# Revit family: Doors_Sliding-Doors_Krownlab_Loki_Single-Sliding-Doors1
name_source: partatom
category: Doors
revit_build: Autodesk Revit 2017 (Build: 20190508_0315(x64)
units: mm (PartAtom-declared; Revit-internal decimal feet)

## family parameters
Always vertical = Yes
Cut with Voids When Loaded = No
Host = Wall
OmniClass Number = 23.30.10.00
OmniClass Title = Doors
Room Calculation Point = No
Shared = No

## types (1)
- Refer to Type Catalog
    Analytic Construction = <None>
    Assembly Code = C1020
    Clnc = 1 1/8"
    Custom Overlap Left = 2"
    Custom Overlap Right = 2"
    Custom Overlap Top = 1 1/4"
    Default Door Thickness = Default Thickness is 1 3/4 inches
    Description = A completely customizable sliding door hardware system with out-of-level and out-of-plum adjustment at every attachment point.
    Door Thickness Restrictions = Top Mount door panel thickness range is: 1-3/8” – 3”. Face Mount door panel thickness range is: 3/4” – 2-1/2”. Glass Mount door panel thickness range is: 3/8” – ½”.
    Edition number = 2
    Face Mount = Default Thickness is 1 3/4 inches
    Function = Interior
    Glass Mount = Default Thickness is 1/2 inch
    Glass Weight Calculation = 0.00 lb
    Height = 90 11/16"
    Lft_Sd_Ctrl = 2"
    Manufacturer = Krownlab
    Model = Loki Single Door
    Mounting Point Spacing = 24"
    Operation = Sliding
    Panel Area = 21.22 ft²
    Panel Height = 84 7/8"
    Panel Material = Wood - Krownlab - Showcase Wood
    Panel Size Availability = Available
    Panel Size Restrictions = Minimum Panel Height is 20”, Minimum Panel Width is 24”.
    Panel Width = 36"
    Product Guid = 76f97f46-7ea8-410c-a3bf-36cbabb0e76b
    Product data url = https://bimobject.com
    Rough Height = 84"
    Rough Width = 32"
    Rt_Sd_Ctrl = 2"
    Standard Glass Weights = 3/8” glass weighs ~5lb/sf. ½” glass weighs ~6.5lb/sf
    Standoff 1 = Krownlab Track Standoff : Solid Wall - 1/4"
    Standoff 2 = Krownlab Track Standoff : Solid Wall - 1"
    Standoff 3 = Krownlab Track Standoff : Glass Wall - 1/4"
    Standoff 4 = Krownlab Track Standoff : Glass Wall - 3/4"
    Standoff 5 = Krownlab Track Standoff : Glass Wall - 1"
    Thickness = 1 3/8"
    Thickness Control = 1 3/8"
    Top Mount = Default Thickness is 1 3/4 inches
    Track Mounting Note = Track mounting point pattern is approximate, and will differ from actual requirements of system.  Maximum single length track is 142”. Multiple tracks can be connected.  Please contact manufacturer for more information.
    Trk_Stp = 3 1/8"
    Trolley Distance From Panel Edge = 4"
    Type Comments = Loki Single Sliding Door
    URL = www.krownlab.com
    Wall Closure = By host
    |_Mt_Opt_01 = No
    |_Mt_Opt_02 = Yes
    |_Pn_Opt_01 = Yes
    |_Pn_Opt_02 = No

## geometry (parser evidence)
native form markers: Sweep x18
no freeform markers — native parametric forms only
